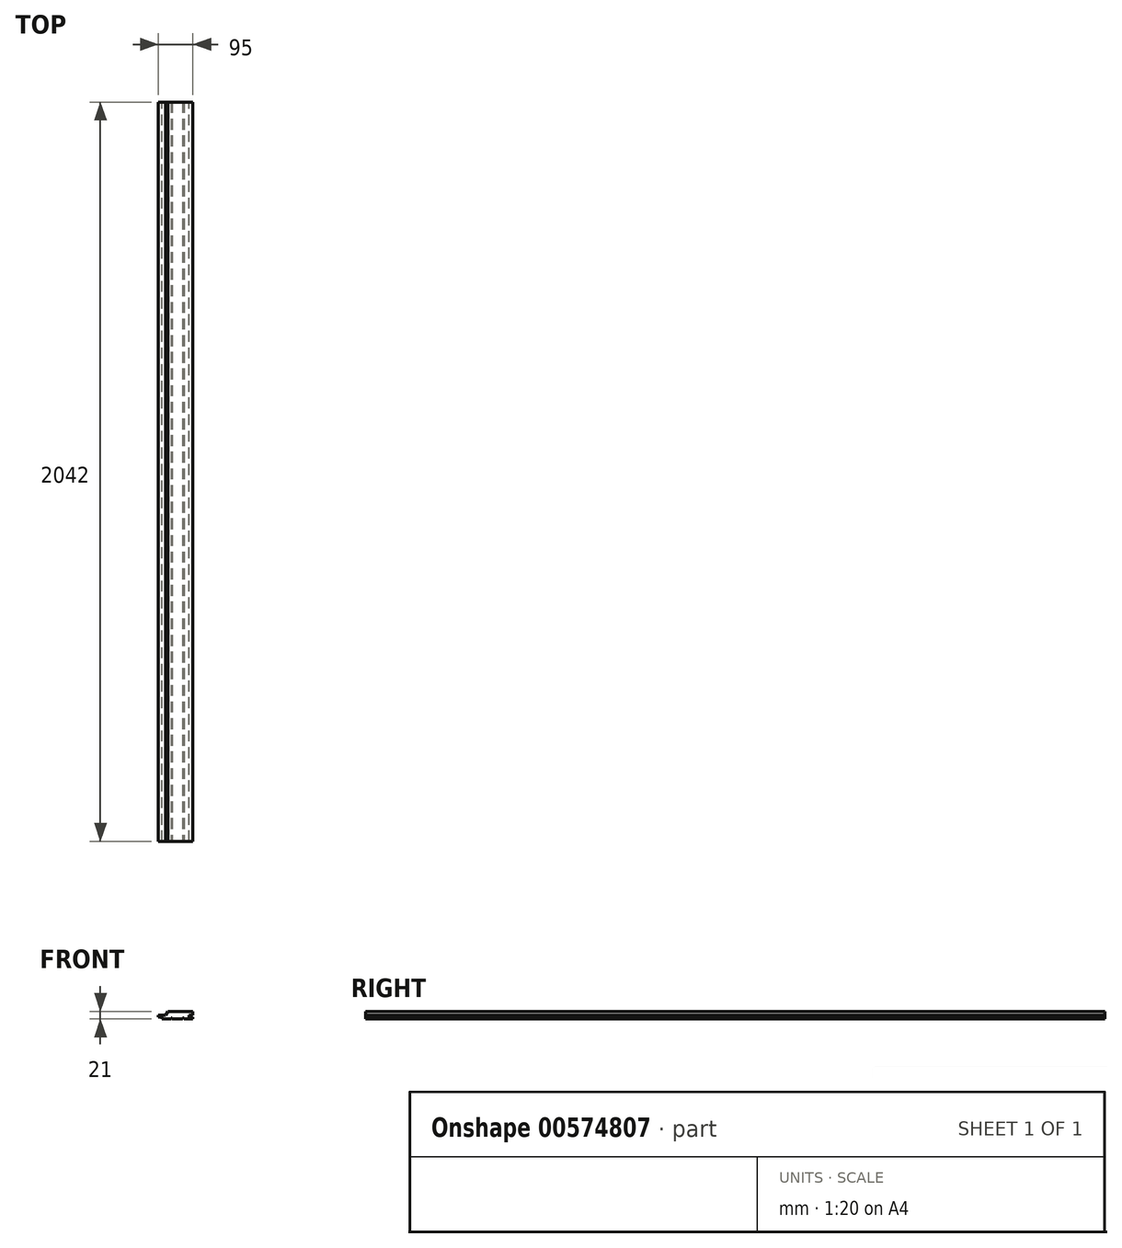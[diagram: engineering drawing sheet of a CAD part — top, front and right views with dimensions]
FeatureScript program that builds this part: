
annotation { "Feature Type Name" : "Feature", "Feature Type Description" : "" }
export const myFeature = defineFeature(function(context is Context, id is Id, definition is map)
    precondition{}
    {
        {
            var Q0;
            Q0=qCreatedBy(makeId("Front.planeOp"),FACE);
            var sketch = newSketch(context, id + "F0", { "sketchPlane" : qUnion([Q0])});
            skLineSegment(sketch, "E0", {"start": v(-21.73, 10.5) * mm, "end": v(47.5, 10.5) * mm});
            skLineSegment(sketch, "E1", {"start": v(47.5, 10.5) * mm, "end": v(47.5, 0.5) * mm});
            skLineSegment(sketch, "E2", {"start": v(47.5, 0.5) * mm, "end": v(37.5, 0.5) * mm});
            skLineSegment(sketch, "E3", {"start": v(37.5, 0.5) * mm, "end": v(37.5, -4.5) * mm});
            skLineSegment(sketch, "E4", {"start": v(37.5, -4.5) * mm, "end": v(47.5, -4.5) * mm});
            skLineSegment(sketch, "E5", {"start": v(47.5, -4.5) * mm, "end": v(47.5, -10.5) * mm});
            skLineSegment(sketch, "E6", {"start": v(47.5, -10.5) * mm, "end": v(-37.5, -10.5) * mm});
            skLineSegment(sketch, "E7", {"start": v(-37.5, -10.5) * mm, "end": v(-37.5, -4.5) * mm});
            skLineSegment(sketch, "E8", {"start": v(-37.5, -4.5) * mm, "end": v(-47.5, -4.5) * mm});
            skLineSegment(sketch, "E9", {"start": v(-47.5, -4.5) * mm, "end": v(-47.5, 0.5) * mm});
            skLineSegment(sketch, "E10", {"start": v(-47.5, 0.5) * mm, "end": v(-27.5, 0.5) * mm});
            skLineSegment(sketch, "E11", {"start": v(-27.5, 0.5) * mm, "end": v(-21.73, 10.5) * mm});
            skSolve(sketch);
        }
        {
            var Q0;
            Q0 = qSketchRegion(id + "F0", true);
            extrude(context, id + "F1", {"entities" : qUnion([Q0]), "depth" : 2042 * mm, "offsetDistance" : 25 * mm});
        }
        {
            var Q0;
            Q0=makeQuery(id+"F1.opExtrude","CAP_FACE",FACE,{"disambiguationData":[OSD([sQuery(id+"F0.wireOp",EDGE,"E0"),sQuery(id+"F0.wireOp",EDGE,"E1"),sQuery(id+"F0.wireOp",EDGE,"E2"),sQuery(id+"F0.wireOp",EDGE,"E3"),sQuery(id+"F0.wireOp",EDGE,"E4"),sQuery(id+"F0.wireOp",EDGE,"E5"),sQuery(id+"F0.wireOp",EDGE,"E6"),sQuery(id+"F0.wireOp",EDGE,"E7"),sQuery(id+"F0.wireOp",EDGE,"E8"),sQuery(id+"F0.wireOp",EDGE,"E9"),sQuery(id+"F0.wireOp",EDGE,"E10"),sQuery(id+"F0.wireOp",EDGE,"E11")])],"isStart":false});
            var sketch = newSketch(context, id + "F2", { "sketchPlane" : qUnion([Q0])});
            skLineSegment(sketch, "E12.bottom", {"start": v(-12.5, -10.5) * mm, "end": v(-9.5, -10.5) * mm});
            skLineSegment(sketch, "E12.top", {"start": v(-12.5, -7.5) * mm, "end": v(-9.5, -7.5) * mm});
            skLineSegment(sketch, "E12.left", {"start": v(-12.5, -10.5) * mm, "end": v(-12.5, -7.5) * mm});
            skLineSegment(sketch, "E12.right", {"start": v(-9.5, -10.5) * mm, "end": v(-9.5, -7.5) * mm});
            skLineSegment(sketch, "E13.bottom", {"start": v(19.5, -10.5) * mm, "end": v(22.5, -10.5) * mm});
            skLineSegment(sketch, "E13.top", {"start": v(19.5, -7.5) * mm, "end": v(22.5, -7.5) * mm});
            skLineSegment(sketch, "E13.left", {"start": v(19.5, -10.5) * mm, "end": v(19.5, -7.5) * mm});
            skLineSegment(sketch, "E13.right", {"start": v(22.5, -10.5) * mm, "end": v(22.5, -7.5) * mm});
            skSolve(sketch);
        }
        {
            var Q0;
            Q0 = qSketchRegion(id + "F2", true);
            extrude(context, id + "F3", {"entities" : qUnion([Q0]), "operationType" : NewBodyOperationType.REMOVE, "endBound" : BoundingType.THROUGH_ALL, "oppositeDirection" : true, "depth" : 25 * mm, "offsetDistance" : 25 * mm});
        }
    });
